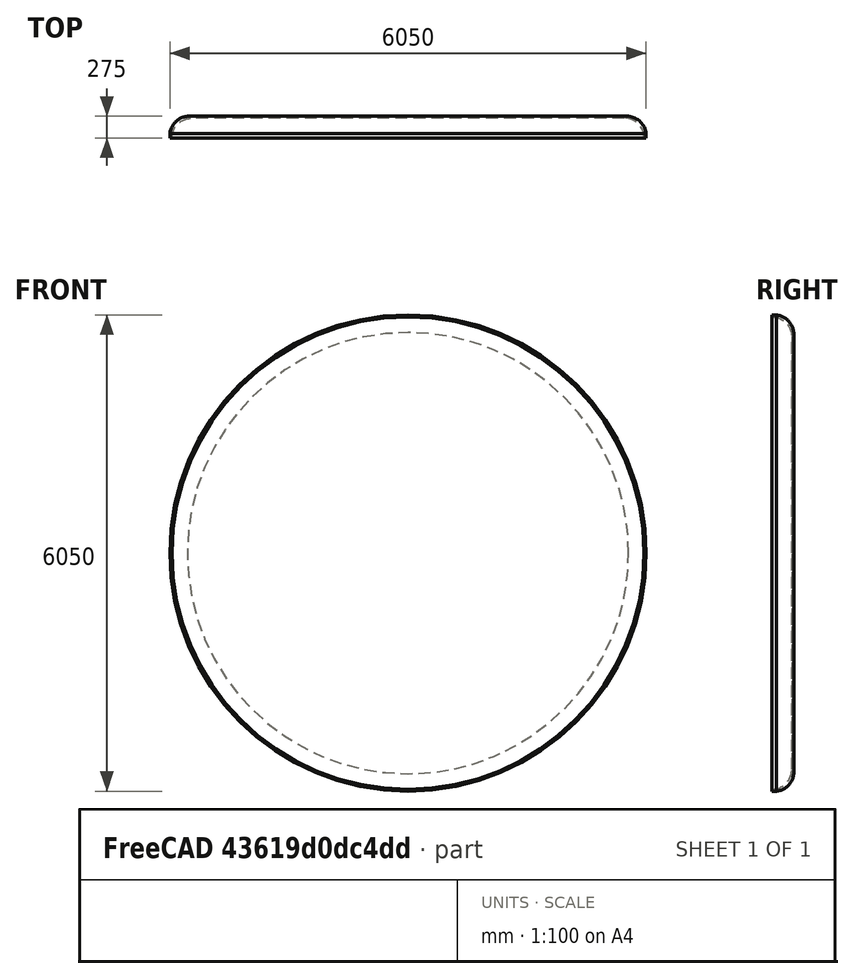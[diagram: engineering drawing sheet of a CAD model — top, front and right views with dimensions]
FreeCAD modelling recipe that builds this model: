
FCSTD DOCUMENT  (FreeCAD 0.21R33771 (Git))
Label: part4(capsule_bottom)
License: All rights reserved
LicenseURL: http://en.wikipedia.org/wiki/All_rights_reserved
objects: Sketcher::SketchObject×1, PartDesign::Revolution×1, PartDesign::Body×1
note: 4 computed .brp shape members not serialized (recipe doc carries the construction recipe); baked Part::Feature solids carry a one-line shape summary decoded from their .brp

FEATURE [Sketcher::SketchObject] Sketch
  FullyConstrained = false
  MapMode = 5
  Support = -> [XY_Plane]
  sketch-geometry (7):
    g0: LineSegment StartX=0 StartY=0 StartZ=0 EndX=2802.8 EndY=-5.68e-14 EndZ=0
    g1: LineSegment StartX=3025 StartY=-222.205 StartZ=0 EndX=3025 EndY=-275 EndZ=0
    g2: LineSegment StartX=3025 StartY=-275 StartZ=0 EndX=3000 EndY=-275 EndZ=0
    g3: LineSegment StartX=2750 StartY=-25 StartZ=0 EndX=0 EndY=-25 EndZ=0
    g4: LineSegment StartX=0 StartY=-25 StartZ=0 EndX=0 EndY=0 EndZ=0
    g5: ArcOfCircle CenterX=2750 CenterY=-275 CenterZ=0 NormalX=0 NormalY=0 NormalZ=1 AngleXU=0 Radius=250 StartAngle=0 EndAngle=1.5708
    g6: ArcOfCircle CenterX=2776.4 CenterY=-248.602 CenterZ=0 NormalX=0 NormalY=0 NormalZ=1 AngleXU=0 Radius=250 StartAngle=0.105787 EndAngle=1.46501
  constraints (17):
    c: Coincident(g-1,g0)
    c: Vertical(g1)
    c: Coincident(g1,g2)
    c: Horizontal(g2)
    c: Horizontal(g3)
    c: Coincident(g3,g4)
    c: Coincident(g4,g0)
    c: Vertical(g4)
    c: DistanceY(g4,g4) = 25
    c: DistanceX(g2,g2) = 25
    c: DistanceX(g3,g2) = 3000
    c: Coincident(g5,g2)
    c: Diameter(g5) = 500
    c: Diameter(g6) = 500
    c: Coincident(g6,g0)
    c: Coincident(g3,g5)
    c: Coincident(g6,g1)
FEATURE [PartDesign::Revolution] Revolution
  Angle = 360
  Axis = (0,1,0)
  Base = (0,0,0)
  Profile = -> Sketch
  ReferenceAxis = -> Sketch [V_Axis]
  Reversed = true
FEATURE [PartDesign::Body] Body
  Group = -> [Sketch,Revolution]
  Origin = -> Origin
  Tip = -> Revolution
